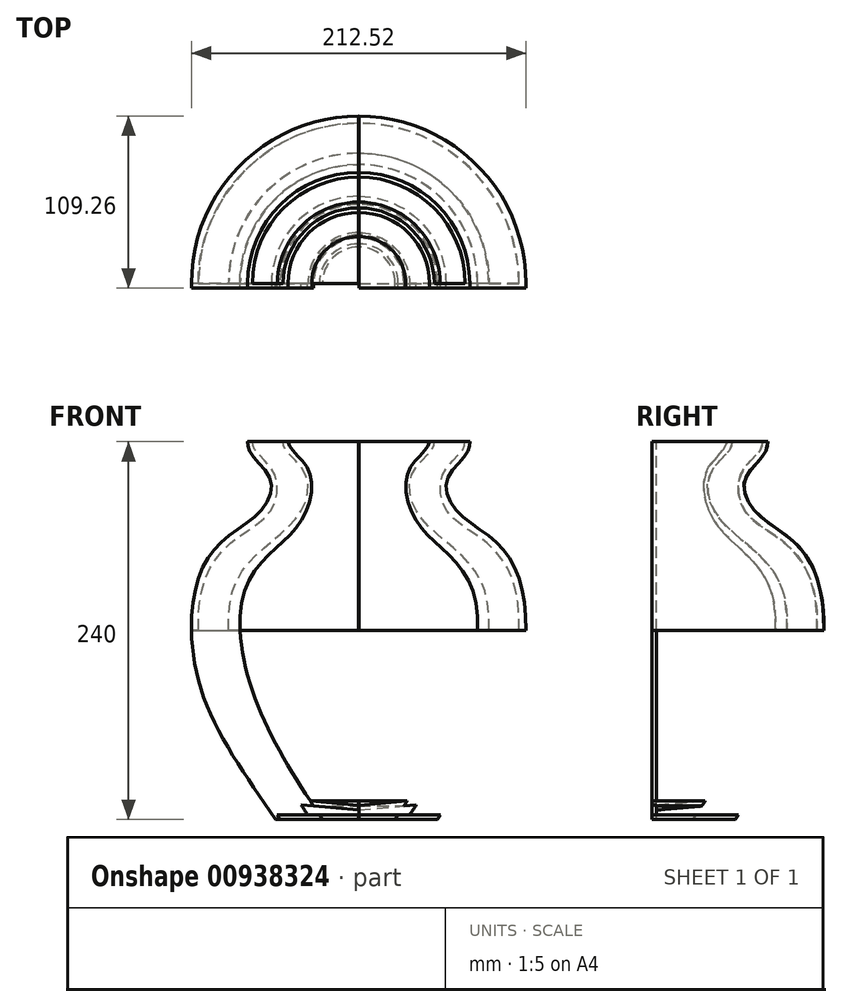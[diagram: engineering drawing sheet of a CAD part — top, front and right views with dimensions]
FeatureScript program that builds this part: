
annotation { "Feature Type Name" : "Feature", "Feature Type Description" : "" }
export const myFeature = defineFeature(function(context is Context, id is Id, definition is map)
    precondition{}
    {
        {
            var Q0;
            Q0=qCreatedBy(makeId("Front.planeOp"),FACE);
            var sketch = newSketch(context, id + "F0", { "sketchPlane" : qUnion([Q0])});
            skLineSegment(sketch, "E0.bottom", {"start": v(0, 0) * mm, "end": v(56, 0) * mm});
            skFitSpline(sketch, "E1", {"points": [v(50, 0) * mm, v(93.5, 78.6) * mm, v(100, 144.02) * mm, v(81.43, 175.57) * mm, v(56.37, 195.52) * mm, v(53.6, 219.65) * mm, v(66.12, 234.96) * mm, v(67.51, 240) * mm], "startDerivative": vector(221.04, 334.2) * mm, "endDerivative": vector(3.61, 84.44) * mm});
            skLineSegment(sketch, "E2", {"start": v(50, 0) * mm, "end": v(53, 0) * mm});
            skLineSegment(sketch, "E3", {"start": v(67.51, 240) * mm, "end": v(70.51, 240) * mm});
            skLineSegment(sketch, "E4.bottom", {"start": v(-0.5, 0) * mm, "end": v(53, 0) * mm});
            skFitSpline(sketch, "E5", {"points": [v(53, 0) * mm, v(99.15, 79.43) * mm, v(104, 144.84) * mm, v(87.94, 175.57) * mm, v(62.88, 195.52) * mm, v(56.04, 215.7) * mm, v(68.67, 232.61) * mm, v(70.51, 240) * mm], "startDerivative": vector(221.04, 334.2) * mm, "endDerivative": vector(3.61, 84.44) * mm});
            skLineSegment(sketch, "E6", {"start": v(53, 0) * mm, "end": v(56, 0) * mm});
            skPoint(sketch, "E7.trimOffspring.end.orphan", {"position": v(106.5, 0) * mm});
            skPoint(sketch, "E7.trimOffspring.start.orphan", {"position": v(100, 0) * mm});
            skLineSegment(sketch, "E8", {"start": v(0, 0) * mm, "end": v(0, 3) * mm});
            skLineSegment(sketch, "E9", {"start": v(0, 3) * mm, "end": v(51.98, 3) * mm});
            skLineSegment(sketch, "E10", {"start": v(30.46, 0) * mm, "end": v(33.46, 0) * mm});
            skLineSegment(sketch, "E11", {"start": v(0, 3) * mm, "end": v(0, 6) * mm});
            skLineSegment(sketch, "E12", {"start": v(0, 6) * mm, "end": v(36.53, 9.2) * mm});
            skFitSpline(sketch, "E13.trimOffspring", {"points": [v(30.46, 0) * mm, v(73.95, 78.6) * mm, v(80.46, 144.02) * mm, v(60.5, 172.1) * mm, v(36.83, 195.52) * mm, v(34.05, 219.65) * mm, v(46.58, 234.96) * mm, v(47.97, 240) * mm], "startDerivative": vector(221.04, 334.2) * mm, "endDerivative": vector(3.61, 84.44) * mm});
            skFitSpline(sketch, "E14.trimOffspring", {"points": [v(23, -0.1) * mm, v(66.5, 78.5) * mm, v(73, 143.92) * mm, v(53.04, 172) * mm, v(34.96, 192.36) * mm, v(30.66, 218.67) * mm, v(40.14, 232.34) * mm, v(44.97, 240.04) * mm], "startDerivative": vector(221.04, 334.2) * mm, "endDerivative": vector(3.61, 84.44) * mm});
            skLineSegment(sketch, "E15", {"start": v(0, 6) * mm, "end": v(0, 9) * mm});
            skLineSegment(sketch, "E16", {"start": v(0, 9) * mm, "end": v(30.76, 11.7) * mm});
            skLineSegment(sketch, "E17", {"start": v(47.97, 240) * mm, "end": v(44.97, 240) * mm});
            skLineSegment(sketch, "E18", {"start": v(0, 0) * mm, "end": v(0, 120) * mm});
            skLineSegment(sketch, "E19", {"start": v(75.37, 120) * mm, "end": v(82.63, 120) * mm});
            skLineSegment(sketch, "E20.trimOffspring", {"start": v(101.74, 120) * mm, "end": v(106.24, 120) * mm});
            skLineSegment(sketch, "E21", {"start": v(47.97, 240) * mm, "end": v(67.51, 240) * mm});
            skLineSegment(sketch, "E22", {"start": v(82.63, 120) * mm, "end": v(101.74, 120) * mm});
            skLineSegment(sketch, "E23.MirrorCS", {"start": v(-67.51, 240) * mm, "end": v(-70.51, 240) * mm});
            skLineSegment(sketch, "E24.MirrorCS", {"start": v(-50, 0) * mm, "end": v(-53, 0) * mm});
            skLineSegment(sketch, "E25.MirrorCS", {"start": v(-47.97, 240) * mm, "end": v(-44.97, 240) * mm});
            skLineSegment(sketch, "E26.MirrorCS", {"start": v(-53, 0) * mm, "end": v(-56, 0) * mm});
            skLineSegment(sketch, "E27.MirrorCS", {"start": v(-101.74, 120) * mm, "end": v(-106.24, 120) * mm});
            skLineSegment(sketch, "E28.MirrorCS", {"start": v(-30.46, 0) * mm, "end": v(-33.46, 0) * mm});
            skLineSegment(sketch, "E29.MirrorCS", {"start": v(-47.97, 240) * mm, "end": v(-67.51, 240) * mm});
            skLineSegment(sketch, "E30.MirrorCS", {"start": v(-75.37, 120) * mm, "end": v(-82.63, 120) * mm});
            skFitSpline(sketch, "E31.MirrorCS", {"points": [v(-50, 0) * mm, v(-93.5, 78.6) * mm, v(-100, 144.02) * mm, v(-81.43, 175.57) * mm, v(-56.37, 195.52) * mm, v(-53.6, 219.65) * mm, v(-66.12, 234.96) * mm, v(-67.51, 240) * mm], "startDerivative": vector(-221.04, 334.2) * mm, "endDerivative": vector(-3.61, 84.44) * mm});
            skFitSpline(sketch, "E32.MirrorCS", {"points": [v(-30.46, 0) * mm, v(-73.95, 78.6) * mm, v(-80.46, 144.02) * mm, v(-60.5, 172.1) * mm, v(-36.83, 195.52) * mm, v(-34.05, 219.65) * mm, v(-46.58, 234.96) * mm, v(-47.97, 240) * mm], "startDerivative": vector(-221.04, 334.2) * mm, "endDerivative": vector(-3.61, 84.44) * mm});
            skFitSpline(sketch, "E33.MirrorCS", {"points": [v(-53, 0) * mm, v(-99.15, 79.43) * mm, v(-104, 144.84) * mm, v(-87.94, 175.57) * mm, v(-62.88, 195.52) * mm, v(-56.04, 215.7) * mm, v(-68.67, 232.61) * mm, v(-70.51, 240) * mm], "startDerivative": vector(-221.04, 334.2) * mm, "endDerivative": vector(-3.61, 84.44) * mm});
            skLineSegment(sketch, "E34.MirrorCS", {"start": v(-82.63, 120) * mm, "end": v(-101.74, 120) * mm});
            skPoint(sketch, "E35.MirrorP", {"position": v(-106.5, 0) * mm});
            skFitSpline(sketch, "E36.MirrorCS", {"points": [v(-23, -0.1) * mm, v(-66.5, 78.5) * mm, v(-73, 143.92) * mm, v(-53.04, 172) * mm, v(-34.96, 192.36) * mm, v(-30.66, 218.67) * mm, v(-40.14, 232.34) * mm, v(-44.97, 240.04) * mm], "startDerivative": vector(-221.04, 334.2) * mm, "endDerivative": vector(-3.61, 84.44) * mm});
            skPoint(sketch, "E37.MirrorP", {"position": v(-100, 0) * mm});
            skLineSegment(sketch, "E38.MirrorCS", {"start": v(0, 9) * mm, "end": v(-30.76, 11.7) * mm});
            skLineSegment(sketch, "E39.MirrorCS", {"start": v(0, 6) * mm, "end": v(-36.53, 9.2) * mm});
            skLineSegment(sketch, "E40.MirrorCS", {"start": v(0, 3) * mm, "end": v(-51.98, 3) * mm});
            skLineSegment(sketch, "E41.MirrorCS", {"start": v(0.5, 0) * mm, "end": v(-53, 0) * mm});
            skSolve(sketch);
        }
        {
            var Q0;
            {var subQ4=sQuery(id+"F0.wireOp",EDGE,"E12");Q0=makeQuery(id+"F0.imprint","IMPRINT",FACE,{"disambiguationData":[TD([[makeQuery(id+"F0.imprint","IMPRINT",EDGE,{"derivedFrom":subQ4}),1.0]])]});}
            var Q1;
            {var subQ7=sQuery(id+"F0.wireOp",EDGE,"E9");Q1=makeQuery(id+"F0.imprint","IMPRINT",FACE,{"disambiguationData":[TD([[makeQuery(id+"F0.imprint","IMPRINT",EDGE,{"derivedFrom":subQ7}),-1.0]])]});}
            var Q2;
            Q2=sQuery(id+"F0.wireOp",EDGE,"E15");
            revolve(context, id + "F1", {"surfaceOperationType" : NewSurfaceOperationType.NEW, "entities" : qUnion([Q0, Q1]), "axis" : qUnion([Q2]), "revolveType" : RevolveType.ONE_DIRECTION, "angle" : 180 * degree});
        }
        {
            var Q0;
            {var subQ0=sQuery(id+"F0.wireOp",EDGE,"E17");Q0=makeQuery(id+"F0.imprint","IMPRINT",FACE,{"disambiguationData":[TD([[makeQuery(id+"F0.imprint","IMPRINT",EDGE,{"derivedFrom":subQ0}),1.0]])]});}
            var Q1;
            {var subQ0=sQuery(id+"F0.wireOp",EDGE,"E3");Q1=makeQuery(id+"F0.imprint","IMPRINT",FACE,{"disambiguationData":[TD([[makeQuery(id+"F0.imprint","IMPRINT",EDGE,{"derivedFrom":subQ0}),-1.0]])]});}
            var Q2;
            Q2=sQuery(id+"F0.wireOp",EDGE,"E18");
            revolve(context, id + "F2", {"surfaceOperationType" : NewSurfaceOperationType.NEW, "entities" : qUnion([Q0, Q1]), "axis" : qUnion([Q2]), "revolveType" : RevolveType.ONE_DIRECTION, "angle" : 180 * degree});
        }
        {
            var Q0;
            {var subQ0=sQuery(id+"F0.wireOp",EDGE,"E21");Q0=makeQuery(id+"F0.imprint","IMPRINT",FACE,{"disambiguationData":[TD([[makeQuery(id+"F0.imprint","IMPRINT",EDGE,{"derivedFrom":subQ0}),-1.0]])]});}
            var Q1;
            {var subQ0=sQuery(id+"F0.wireOp",EDGE,"E17");Q1=makeQuery(id+"F0.imprint","IMPRINT",FACE,{"disambiguationData":[TD([[makeQuery(id+"F0.imprint","IMPRINT",EDGE,{"derivedFrom":subQ0}),1.0]])]});}
            var Q2;
            {var subQ0=sQuery(id+"F0.wireOp",EDGE,"E3");Q2=makeQuery(id+"F0.imprint","IMPRINT",FACE,{"disambiguationData":[TD([[makeQuery(id+"F0.imprint","IMPRINT",EDGE,{"derivedFrom":subQ0}),-1.0]])]});}
            var Q3;
            {var subQ0=sQuery(id+"F0.wireOp",EDGE,"E25.MirrorCS");Q3=makeQuery(id+"F0.imprint","IMPRINT",FACE,{"disambiguationData":[TD([[makeQuery(id+"F0.imprint","IMPRINT",EDGE,{"derivedFrom":subQ0}),-1.0]])]});}
            var Q4;
            {var subQ0=sQuery(id+"F0.wireOp",EDGE,"E29.MirrorCS");Q4=makeQuery(id+"F0.imprint","IMPRINT",FACE,{"disambiguationData":[TD([[makeQuery(id+"F0.imprint","IMPRINT",EDGE,{"derivedFrom":subQ0}),1.0]])]});}
            var Q5;
            {var subQ0=sQuery(id+"F0.wireOp",EDGE,"E23.MirrorCS");Q5=makeQuery(id+"F0.imprint","IMPRINT",FACE,{"disambiguationData":[TD([[makeQuery(id+"F0.imprint","IMPRINT",EDGE,{"derivedFrom":subQ0}),1.0]])]});}
            extrude(context, id + "F3", {"entities" : qUnion([Q0, Q1, Q2, Q3, Q4, Q5]), "operationType" : NewBodyOperationType.ADD, "depth" : 3 * mm, "offsetDistance" : 25 * mm});
        }
        {
            var Q0;
            {var subQ3=sQuery(id+"F0.wireOp",EDGE,"E27.MirrorCS");Q0=makeQuery(id+"F0.imprint","IMPRINT",FACE,{"disambiguationData":[TD([[makeQuery(id+"F0.imprint","IMPRINT",EDGE,{"derivedFrom":subQ3}),1.0]])]});}
            var Q1;
            {var subQ0=sQuery(id+"F0.wireOp",EDGE,"E34.MirrorCS");Q1=makeQuery(id+"F0.imprint","IMPRINT",FACE,{"disambiguationData":[TD([[makeQuery(id+"F0.imprint","IMPRINT",EDGE,{"derivedFrom":subQ0}),1.0]])]});}
            var Q2;
            {var subQ1=sQuery(id+"F0.wireOp",EDGE,"E30.MirrorCS");Q2=makeQuery(id+"F0.imprint","IMPRINT",FACE,{"disambiguationData":[TD([[makeQuery(id+"F0.imprint","IMPRINT",EDGE,{"derivedFrom":subQ1}),1.0]])]});}
            var Q3;
            {var subQ4=sQuery(id+"F0.wireOp",EDGE,"E12");Q3=makeQuery(id+"F0.imprint","IMPRINT",FACE,{"disambiguationData":[TD([[makeQuery(id+"F0.imprint","IMPRINT",EDGE,{"derivedFrom":subQ4}),1.0]])]});}
            var Q4;
            {var subQ3=sQuery(id+"F0.wireOp",EDGE,"E9");Q4=makeQuery(id+"F0.imprint","IMPRINT",FACE,{"disambiguationData":[TD([[makeQuery(id+"F0.imprint","IMPRINT",EDGE,{"derivedFrom":subQ3}),1.0]])]});}
            var Q5;
            {var subQ7=sQuery(id+"F0.wireOp",EDGE,"E9");Q5=makeQuery(id+"F0.imprint","IMPRINT",FACE,{"disambiguationData":[TD([[makeQuery(id+"F0.imprint","IMPRINT",EDGE,{"derivedFrom":subQ7}),-1.0]])]});}
            extrude(context, id + "F4", {"entities" : qUnion([Q0, Q1, Q2, Q3, Q4, Q5]), "operationType" : NewBodyOperationType.ADD, "depth" : 3 * mm, "offsetDistance" : 25 * mm});
        }
        {
            var Q0;
            Q0=qCreatedBy(makeId("Front.planeOp"),FACE);
            var sketch = newSketch(context, id + "F5", { "sketchPlane" : qUnion([Q0])});
            skLineSegment(sketch, "E42.bottom", {"start": v(0, 0) * mm, "end": v(0.1, 0) * mm});
            skLineSegment(sketch, "E42.top", {"start": v(0, 250) * mm, "end": v(0.1, 250) * mm});
            skLineSegment(sketch, "E42.left", {"start": v(0, 0) * mm, "end": v(0, 250) * mm});
            skLineSegment(sketch, "E42.right", {"start": v(0.1, 0) * mm, "end": v(0.1, 250) * mm});
            skSolve(sketch);
        }
        {
            var Q0;
            Q0=makeQuery(id+"F5.imprint","IMPRINT",FACE,{"disambiguationData":[TD([[makeQuery(id+"F5.imprint","IMPRINT",EDGE,{"derivedFrom":sQuery(id+"F5.wireOp",EDGE,"E42.bottom")}),1.0]])]});
            extrude(context, id + "F6", {"entities" : qUnion([Q0]), "operationType" : NewBodyOperationType.REMOVE, "endBound" : BoundingType.SYMMETRIC, "oppositeDirection" : true, "depth" : 505 * mm, "offsetDistance" : 25 * mm});
        }
    });
